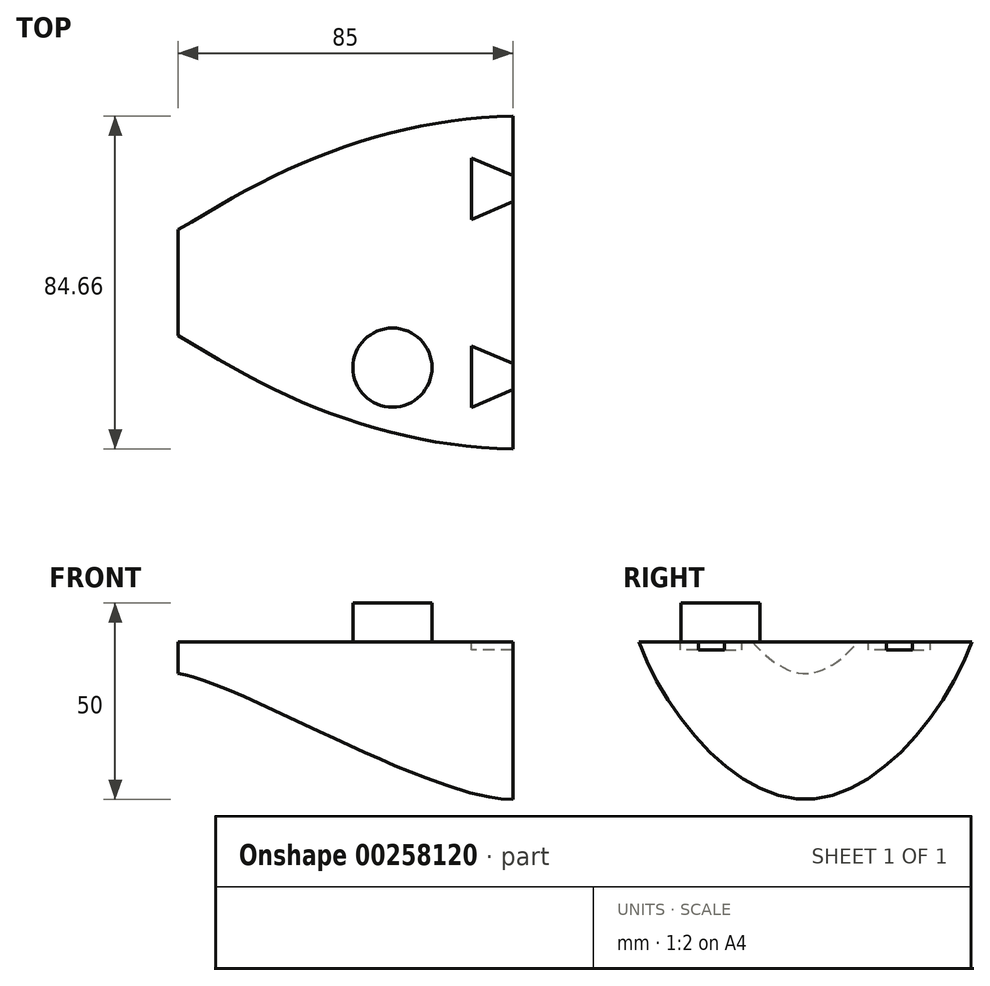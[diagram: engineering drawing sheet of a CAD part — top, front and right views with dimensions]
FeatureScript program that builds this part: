
annotation { "Feature Type Name" : "Feature", "Feature Type Description" : "" }
export const myFeature = defineFeature(function(context is Context, id is Id, definition is map)
    precondition{}
    {
        {
            var Q0;
            Q0=qCreatedBy(makeId("Right.planeOp"),FACE);
            cPlane(context, id + "F0", {"entities" : qUnion([Q0]), "cplaneType" : CPlaneType.OFFSET, "offset" : 85 * mm, "oppositeDirection" : true, "width" : 152.4 * mm, "height" : 152.4 * mm});
        }
        {
            var Q0;
            Q0=qCreatedBy(makeId("Right.planeOp"),FACE);
            var sketch = newSketch(context, id + "F1", { "sketchPlane" : qUnion([Q0])});
            skFitSpline(sketch, "E0", {"points": [v(-45, 0) * mm, v(0, -50) * mm, v(45, 0) * mm], "startDerivative": vector(18, -120) * mm, "endDerivative": vector(18, 120) * mm});
            skLineSegment(sketch, "E1", {"start": v(-45, 0) * mm, "end": v(45, 0) * mm});
            skSolve(sketch);
        }
        {
            var Q0;
            Q0=qCreatedBy(id+"F0.planeOp",FACE);
            var sketch = newSketch(context, id + "F2", { "sketchPlane" : qUnion([Q0])});
            skFitSpline(sketch, "E2", {"points": [v(-20, 0) * mm, v(0, -18) * mm, v(20, 0) * mm], "startDerivative": vector(12, -30) * mm, "endDerivative": vector(12, 30) * mm});
            skLineSegment(sketch, "E3", {"start": v(-20, 0) * mm, "end": v(20, 0) * mm});
            skSolve(sketch);
        }
        {
            var Q0;
            Q0=qCreatedBy(makeId("Front.planeOp"),FACE);
            var sketch = newSketch(context, id + "F3", { "sketchPlane" : qUnion([Q0])});
            skFitSpline(sketch, "E4", {"points": [v(-85, -18) * mm, v(0, -50) * mm], "startDerivative": vector(45, -6) * mm, "endDerivative": vector(63.55, 0) * mm});
            skSolve(sketch);
        }
        {
            var Q0;
            Q0=qCreatedBy(makeId("Top.planeOp"),FACE);
            var sketch = newSketch(context, id + "F4", { "sketchPlane" : qUnion([Q0])});
            skFitSpline(sketch, "E5", {"points": [v(-85, 20) * mm, v(0, 45) * mm], "startDerivative": vector(60, 36) * mm, "endDerivative": vector(105, 0) * mm});
            skFitSpline(sketch, "E6", {"points": [v(-85, -20) * mm, v(0, -45) * mm], "startDerivative": vector(60, -36) * mm, "endDerivative": vector(105, 0) * mm});
            skSolve(sketch);
        }
        {
            var Q0;
            Q0=makeQuery(id+"F1.imprint","IMPRINT",FACE,{"disambiguationData":[TD([[makeQuery(id+"F1.imprint","IMPRINT",EDGE,{"derivedFrom":sQuery(id+"F1.wireOp",EDGE,"E0")}),1.0]])]});
            var Q1;
            Q1=makeQuery(id+"F2.imprint","IMPRINT",FACE,{"disambiguationData":[TD([[makeQuery(id+"F2.imprint","IMPRINT",EDGE,{"derivedFrom":sQuery(id+"F2.wireOp",EDGE,"E2")}),1.0]])]});
            var Q2;
            Q2=sQuery(id+"F4.wireOp",EDGE,"E5");
            var Q3;
            Q3=sQuery(id+"F3.wireOp",EDGE,"E4");
            var Q4;
            Q4=sQuery(id+"F4.wireOp",EDGE,"E6");
            loft(context, id + "F5", {"addGuides" : true, "sheetProfilesArray" : [{ "sheetProfileEntities" : qUnion([Q0]) }, { "sheetProfileEntities" : qUnion([Q1]) }], "guidesArray" : [{ "guideEntities" : qUnion([Q2]), "guideDerivativeType" : LoftGuideDerivativeType.DEFAULT, "guideDerivativeMagnitude" : 1 }, { "guideEntities" : qUnion([Q3]), "guideDerivativeType" : LoftGuideDerivativeType.DEFAULT, "guideDerivativeMagnitude" : 1 }, { "guideEntities" : qUnion([Q4]), "guideDerivativeType" : LoftGuideDerivativeType.DEFAULT, "guideDerivativeMagnitude" : 1 }]});
        }
        {
            var Q0;
            Q0=qCreatedBy(makeId("Top.planeOp"),FACE);
            var sketch = newSketch(context, id + "F6", { "sketchPlane" : qUnion([Q0])});
            skLineSegment(sketch, "E7", {"start": v(-10.44, 23.89) * mm, "end": v(13.73, 23.89) * mm, "construction": true});
            skLineSegment(sketch, "E8.MirrorCS", {"start": v(-10.44, -23.89) * mm, "end": v(13.73, -23.89) * mm, "construction": true});
            skLineSegment(sketch, "E9", {"start": v(0, 27.17) * mm, "end": v(0, 23.89) * mm});
            skLineSegment(sketch, "E10", {"start": v(0, 27.17) * mm, "end": v(-10.44, 31.7) * mm});
            skLineSegment(sketch, "E11", {"start": v(-10.44, 31.7) * mm, "end": v(-10.44, 23.89) * mm});
            skLineSegment(sketch, "E12.MirrorCS", {"start": v(0, 20.6) * mm, "end": v(-10.44, 16.07) * mm});
            skLineSegment(sketch, "E13.MirrorCS", {"start": v(-10.44, 16.07) * mm, "end": v(-10.44, 23.89) * mm});
            skLineSegment(sketch, "E14.MirrorCS", {"start": v(0, 20.6) * mm, "end": v(0, 23.89) * mm});
            skLineSegment(sketch, "E15.MirrorCS", {"start": v(0, -20.6) * mm, "end": v(-10.44, -16.07) * mm});
            skLineSegment(sketch, "E16.MirrorCS", {"start": v(-10.44, -16.07) * mm, "end": v(-10.44, -23.89) * mm});
            skLineSegment(sketch, "E17.MirrorCS", {"start": v(-10.44, -31.7) * mm, "end": v(-10.44, -23.89) * mm});
            skLineSegment(sketch, "E18.MirrorCS", {"start": v(0, -27.17) * mm, "end": v(-10.44, -31.7) * mm});
            skLineSegment(sketch, "E19.MirrorCS", {"start": v(0, -27.17) * mm, "end": v(0, -23.89) * mm});
            skLineSegment(sketch, "E20.MirrorCS", {"start": v(0, -20.6) * mm, "end": v(0, -23.89) * mm});
            skLineSegment(sketch, "E21", {"start": v(0, 23.89) * mm, "end": v(0, 20.6) * mm});
            skLineSegment(sketch, "E22", {"start": v(-10.44, 23.89) * mm, "end": v(-10.44, 16.07) * mm});
            skLineSegment(sketch, "E23", {"start": v(0, 23.89) * mm, "end": v(0, 27.17) * mm});
            skLineSegment(sketch, "E24", {"start": v(-10.44, -23.89) * mm, "end": v(-10.44, -31.7) * mm});
            skLineSegment(sketch, "E25", {"start": v(-10.44, -31.7) * mm, "end": v(0, -27.17) * mm});
            skSolve(sketch);
        }
        {
            var Q0;
            Q0=makeQuery(id+"F6.imprint","IMPRINT",FACE,{"disambiguationData":[TD([[makeQuery(id+"F6.imprint","IMPRINT",EDGE,{"derivedFrom":sQuery(id+"F6.wireOp",EDGE,"E10")}),1.0]])]});
            var Q1;
            Q1=makeQuery(id+"F6.imprint","IMPRINT",FACE,{"disambiguationData":[TD([[makeQuery(id+"F6.imprint","IMPRINT",EDGE,{"derivedFrom":sQuery(id+"F6.wireOp",EDGE,"E19.MirrorCS")}),1.0]])]});
            extrude(context, id + "F7", {"entities" : qUnion([Q0, Q1]), "operationType" : NewBodyOperationType.REMOVE, "oppositeDirection" : true, "depth" : 12 * mm});
        }
        {
            var Q0;
            Q0=makeQuery(id+"F5.opLoft","SWEPT_FACE",FACE,{"disambiguationData":[OSD([sQuery(id+"F1.wireOp",EDGE,"E1"),sQuery(id+"F2.wireOp",EDGE,"E3"),sQuery(id+"F4.wireOp",EDGE,"E5"),sQuery(id+"F4.wireOp",EDGE,"E6")])]});
            var sketch = newSketch(context, id + "F8", { "sketchPlane" : qUnion([Q0])});
            skCircle(sketch, "E26", {"center": v(-30.58, 21.6) * mm, "radius": 10.05 * mm});
            skCircle(sketch, "E27.MirrorC", {"center": v(-30.58, -21.6) * mm, "radius": 10.05 * mm});
            skSolve(sketch);
        }
        {
            var Q0;
            Q0=makeQuery(id+"F8.imprint","IMPRINT",FACE,{"disambiguationData":[TD([[makeQuery(id+"F8.imprint","IMPRINT",EDGE,{"derivedFrom":sQuery(id+"F8.wireOp",EDGE,"E26")}),1.0]])]});
            var Q1;
            Q1=makeQuery(id+"F8.imprint","IMPRINT",FACE,{"disambiguationData":[TD([[makeQuery(id+"F8.imprint","IMPRINT",EDGE,{"derivedFrom":sQuery(id+"F8.wireOp",EDGE,"E27.MirrorC")}),-1.0]])]});
            extrude(context, id + "F9", {"entities" : qUnion([Q0, Q1]), "operationType" : NewBodyOperationType.REMOVE, "oppositeDirection" : true, "depth" : 10 * mm});
        }
    });
